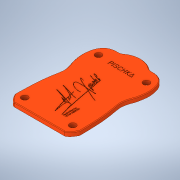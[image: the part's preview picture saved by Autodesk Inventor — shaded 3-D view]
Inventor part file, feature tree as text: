
AUTODESK INVENTOR PART (.ipt)
format: ipt  version: 2020.1 (Build 241239000, 239)  size: 2,935,808 bytes
history: native  units: mm
features: sketch x4, extrude x2, emboss x2, chamfer x1
ambient origin geometry x8: Origin, YZ Plane, XZ Plane, XY Plane, X Axis, Y Axis, Z Axis, Center Point
bodies: Solid1 (feature_tree)
feature tree (9):
  extrude  "Extrusion1"  Depth=0.5mm TaperAngle=0.0deg
  sketch  "Sketch2"  dims[d28=0.5mm d29=2.0mm d30=45.0deg d31=0.8mm d32=0.0mm d33=0.4mm d34=0.0mm]
  extrude  "Extrusion3"  Depth=0.4mm TaperAngle=0.0deg
  chamfer  "Chamfer1"  Distance=0.4mm
  emboss  "Emboss2"
  emboss  "Emboss3"
  sketch  "Sketch1"  dims[d0=3.5mm d1=0.0mm d26=0.5mm d27=0.0mm]
  sketch  "Sketch4"
  sketch  "Sketch5"
